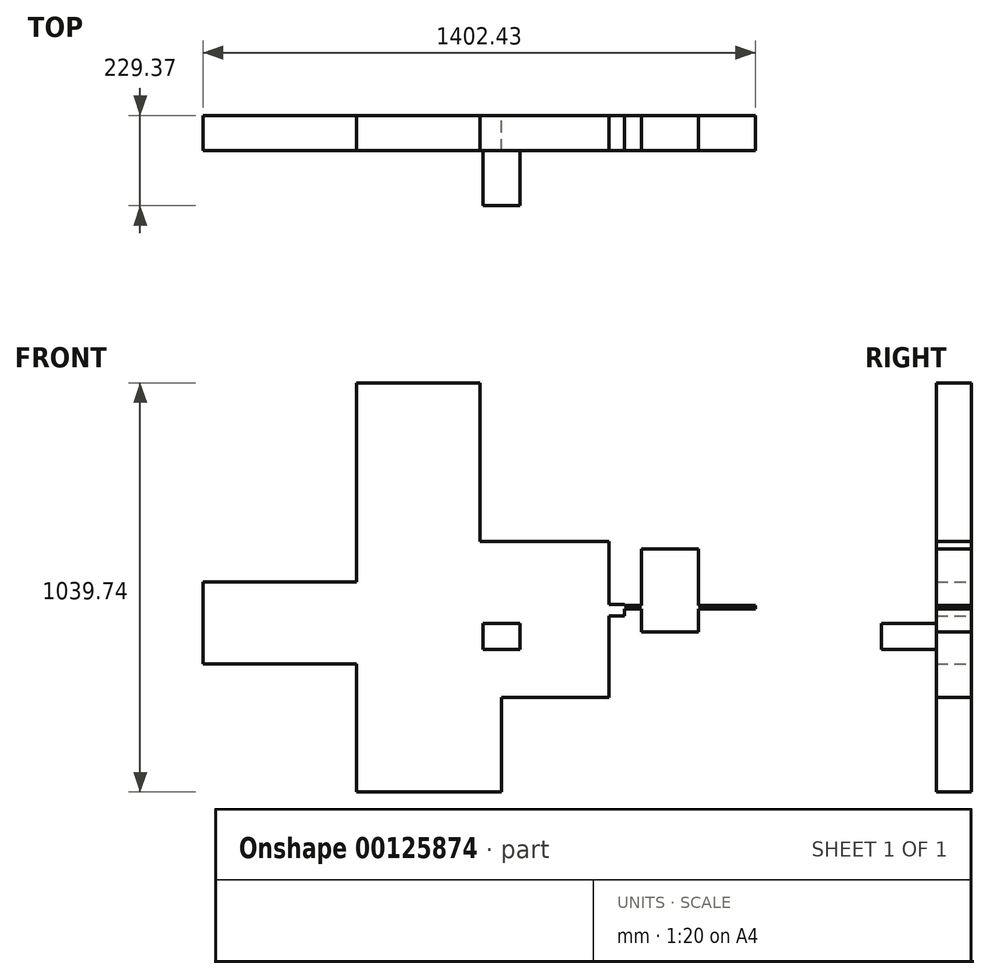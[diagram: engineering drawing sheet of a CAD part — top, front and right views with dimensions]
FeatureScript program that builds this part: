
annotation { "Feature Type Name" : "Feature", "Feature Type Description" : "" }
export const myFeature = defineFeature(function(context is Context, id is Id, definition is map)
    precondition{}
    {
        {
            var Q0;
            Q0=qCreatedBy(makeId("Front.planeOp"),FACE);
            var sketch = newSketch(context, id + "F0", { "sketchPlane" : qUnion([Q0])});
            skLineSegment(sketch, "E0.bottom", {"start": v(61.7, 122.82) * mm, "end": v(-33.08, 122.82) * mm});
            skLineSegment(sketch, "E0.top", {"start": v(61.7, 188.85) * mm, "end": v(-33.08, 188.85) * mm});
            skLineSegment(sketch, "E0.left", {"start": v(61.7, 122.82) * mm, "end": v(61.7, 188.85) * mm});
            skLineSegment(sketch, "E0.right", {"start": v(-33.08, 122.82) * mm, "end": v(-33.08, 188.85) * mm});
            skSolve(sketch);
        }
        {
            var Q0;
            Q0 = qSketchRegion(id + "F0", true);
            extrude(context, id + "F1", {"entities" : qUnion([Q0]), "depth" : 229.37 * mm});
        }
        {
            var Q0;
            Q0=qCreatedBy(makeId("Front.planeOp"),FACE);
            var sketch = newSketch(context, id + "F2", { "sketchPlane" : qUnion([Q0])});
            skLineSegment(sketch, "E1.bottom", {"start": v(13.8, 0) * mm, "end": v(-354.07, 0) * mm});
            skLineSegment(sketch, "E1.top", {"start": v(13.8, -239.85) * mm, "end": v(-354.07, -239.85) * mm});
            skLineSegment(sketch, "E1.left", {"start": v(13.8, 0) * mm, "end": v(13.8, -239.85) * mm});
            skLineSegment(sketch, "E1.right", {"start": v(-354.07, 0) * mm, "end": v(-354.07, -239.85) * mm});
            skLineSegment(sketch, "E2.bottom", {"start": v(-354.07, 0) * mm, "end": v(287.54, 0) * mm});
            skLineSegment(sketch, "E2.top", {"start": v(-354.07, 397.2) * mm, "end": v(287.54, 397.2) * mm});
            skLineSegment(sketch, "E2.left", {"start": v(-354.07, 0) * mm, "end": v(-354.07, 397.2) * mm});
            skLineSegment(sketch, "E2.right", {"start": v(287.54, 0) * mm, "end": v(287.54, 397.2) * mm});
            skLineSegment(sketch, "E3.bottom", {"start": v(-354.07, 397.2) * mm, "end": v(-39.67, 397.2) * mm});
            skLineSegment(sketch, "E3.top", {"start": v(-354.07, 799.9) * mm, "end": v(-39.67, 799.9) * mm});
            skLineSegment(sketch, "E3.left", {"start": v(-354.07, 397.2) * mm, "end": v(-354.07, 799.9) * mm});
            skLineSegment(sketch, "E3.right", {"start": v(-39.67, 397.2) * mm, "end": v(-39.67, 799.9) * mm});
            skLineSegment(sketch, "E4.bottom", {"start": v(326.21, 225.23) * mm, "end": v(659, 225.23) * mm});
            skLineSegment(sketch, "E4.top", {"start": v(326.21, 234.34) * mm, "end": v(659, 234.34) * mm});
            skLineSegment(sketch, "E4.left", {"start": v(326.21, 225.23) * mm, "end": v(326.21, 234.34) * mm});
            skLineSegment(sketch, "E4.right", {"start": v(659, 225.23) * mm, "end": v(659, 234.34) * mm});
            skLineSegment(sketch, "E5.bottom", {"start": v(326.21, 236.51) * mm, "end": v(287.54, 236.51) * mm});
            skLineSegment(sketch, "E5.top", {"start": v(326.21, 207.28) * mm, "end": v(287.54, 207.28) * mm});
            skLineSegment(sketch, "E5.left", {"start": v(326.21, 236.51) * mm, "end": v(326.21, 207.28) * mm});
            skLineSegment(sketch, "E5.right", {"start": v(287.54, 236.51) * mm, "end": v(287.54, 207.28) * mm});
            skLineSegment(sketch, "E6.bottom", {"start": v(369.59, 166.57) * mm, "end": v(514.63, 166.57) * mm});
            skLineSegment(sketch, "E6.top", {"start": v(369.59, 377.57) * mm, "end": v(514.63, 377.57) * mm});
            skLineSegment(sketch, "E6.left", {"start": v(369.59, 166.57) * mm, "end": v(369.59, 377.57) * mm});
            skLineSegment(sketch, "E6.right", {"start": v(514.63, 166.57) * mm, "end": v(514.63, 377.57) * mm});
            skLineSegment(sketch, "E7.bottom", {"start": v(-354.07, 86.18) * mm, "end": v(-743.42, 86.18) * mm});
            skLineSegment(sketch, "E7.top", {"start": v(-354.07, 293.83) * mm, "end": v(-743.42, 293.83) * mm});
            skLineSegment(sketch, "E7.left", {"start": v(-354.07, 86.18) * mm, "end": v(-354.07, 293.83) * mm});
            skLineSegment(sketch, "E7.right", {"start": v(-743.42, 86.18) * mm, "end": v(-743.42, 293.83) * mm});
            skSolve(sketch);
        }
        {
            var Q0;
            Q0 = qSketchRegion(id + "F2", true);
            extrude(context, id + "F3", {"entities" : qUnion([Q0]), "operationType" : NewBodyOperationType.ADD, "depth" : 89.5 * mm});
        }
    });
